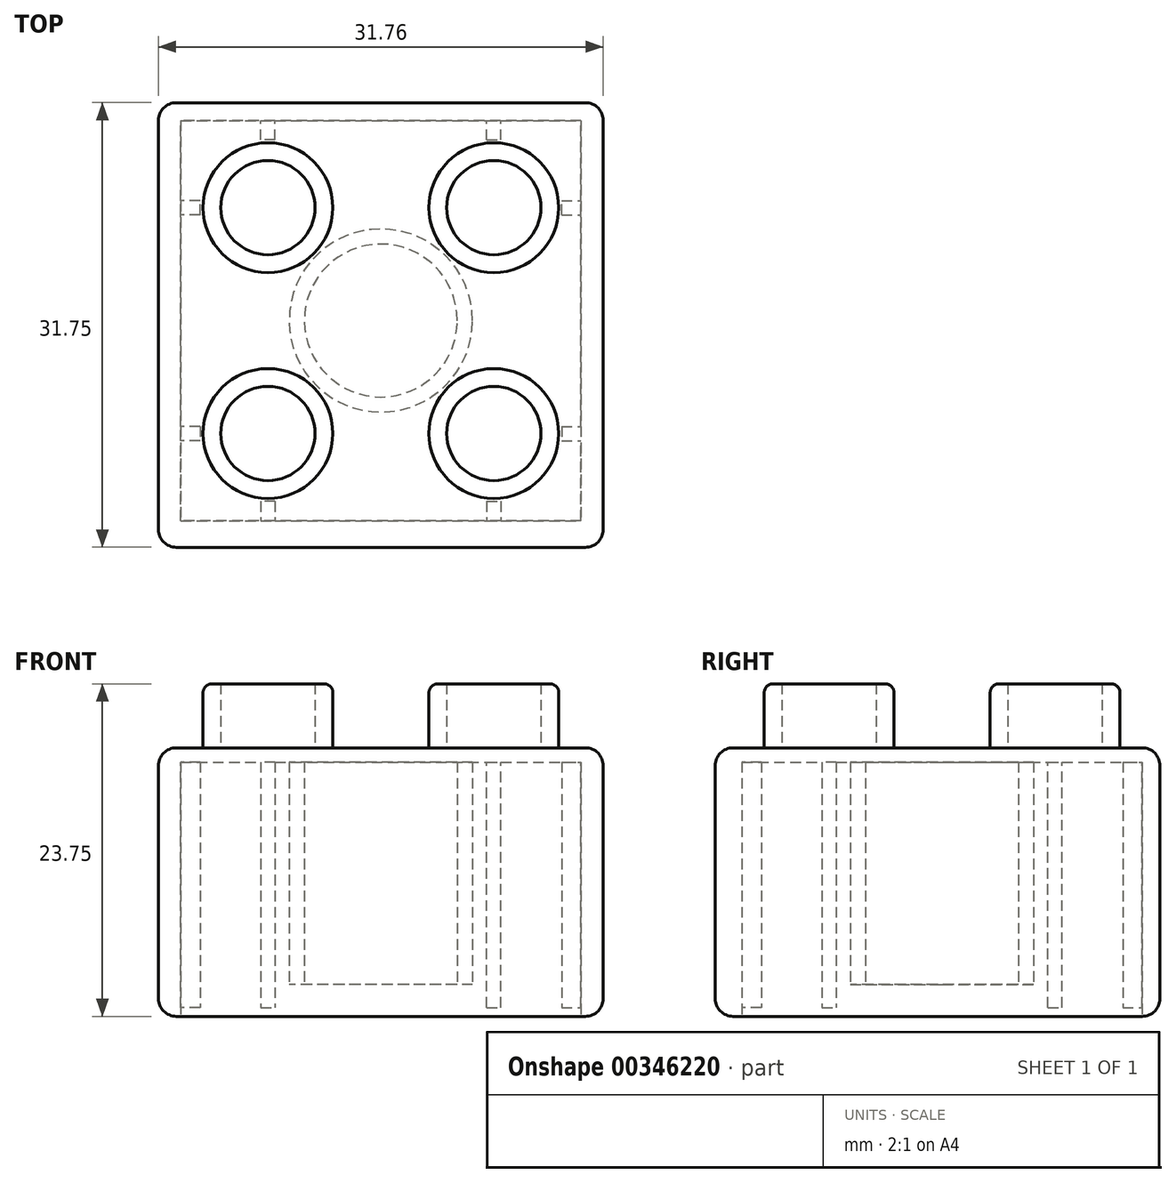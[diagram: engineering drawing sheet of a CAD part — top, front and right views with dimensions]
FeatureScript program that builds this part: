
annotation { "Feature Type Name" : "Feature", "Feature Type Description" : "" }
export const myFeature = defineFeature(function(context is Context, id is Id, definition is map)
    precondition{}
    {
        {
            var Q0;
            Q0=qCreatedBy(makeId("Top.planeOp"),FACE);
            var sketch = newSketch(context, id + "F0", { "sketchPlane" : qUnion([Q0])});
            skPoint(sketch, "E0", {"position": v(0, 16.87) * mm});
            skPoint(sketch, "E1", {"position": v(0, 15.88) * mm});
            skPoint(sketch, "E2", {"position": v(0, -14.88) * mm});
            skPoint(sketch, "E3", {"position": v(0, -15.88) * mm});
            skPoint(sketch, "E4", {"position": v(17.1, 0) * mm});
            skPoint(sketch, "E5", {"position": v(15.88, 0) * mm});
            skPoint(sketch, "E6", {"position": v(-15.88, 0) * mm});
            skPoint(sketch, "E7", {"position": v(15.64, 15.88) * mm});
            skPoint(sketch, "E8", {"position": v(15.88, 15.56) * mm});
            skPoint(sketch, "E9", {"position": v(-16.3, -15.88) * mm});
            skPoint(sketch, "E10", {"position": v(-15.88, -16.2) * mm});
            skLineSegment(sketch, "E11.bottom", {"start": v(-15.88, -16.2) * mm, "end": v(15.88, -16.2) * mm});
            skLineSegment(sketch, "E11.top", {"start": v(-15.88, 15.56) * mm, "end": v(15.88, 15.56) * mm});
            skLineSegment(sketch, "E11.left", {"start": v(-15.88, -16.2) * mm, "end": v(-15.88, 15.56) * mm});
            skLineSegment(sketch, "E11.right", {"start": v(15.88, -16.2) * mm, "end": v(15.88, 15.56) * mm});
            skSolve(sketch);
        }
        {
            var Q0;
            Q0=makeQuery(id+"F0.imprint","IMPRINT",FACE,{"disambiguationData":[TD([[makeQuery(id+"F0.imprint","IMPRINT",EDGE,{"derivedFrom":sQuery(id+"F0.wireOp",EDGE,"E11.bottom")}),1.0]])]});
            var sketch = newSketch(context, id + "F1", { "sketchPlane" : qUnion([Q0])});
            skPoint(sketch, "E12", {"position": v(14.77, 0) * mm});
            skPoint(sketch, "E13", {"position": v(14.29, 0) * mm});
            skPoint(sketch, "E14", {"position": v(-14.29, 0) * mm});
            skPoint(sketch, "E15", {"position": v(-14.29, -14.92) * mm});
            skPoint(sketch, "E16", {"position": v(-14.29, -14.29) * mm});
            skPoint(sketch, "E17", {"position": v(14.29, 14.33) * mm});
            skPoint(sketch, "E18", {"position": v(14.29, 14.29) * mm});
            skLineSegment(sketch, "E19.bottom", {"start": v(-14.29, -14.29) * mm, "end": v(14.29, -14.29) * mm});
            skLineSegment(sketch, "E19.top", {"start": v(-14.29, 14.29) * mm, "end": v(14.29, 14.29) * mm});
            skLineSegment(sketch, "E19.left", {"start": v(-14.29, -14.29) * mm, "end": v(-14.29, 14.29) * mm});
            skLineSegment(sketch, "E19.right", {"start": v(14.29, -14.29) * mm, "end": v(14.29, 14.29) * mm});
            skSolve(sketch);
        }
        {
            var Q0;
            Q0=makeQuery(id+"F1.imprint","IMPRINT",FACE,{"disambiguationData":[TD([[makeQuery(id+"F1.imprint","IMPRINT",EDGE,{"derivedFrom":sQuery(id+"F1.wireOp",EDGE,"E19.bottom")}),1.0]])]});
            var sketch = newSketch(context, id + "F2", { "sketchPlane" : qUnion([Q0])});
            skPoint(sketch, "E20", {"position": v(0, 0) * mm});
            skCircle(sketch, "E21", {"center": v(0, 0) * mm, "radius": 6.54 * mm});
            skSolve(sketch);
        }
        {
            var Q0;
            Q0=makeQuery(id+"F1.imprint","IMPRINT",FACE,{"disambiguationData":[TD([[makeQuery(id+"F1.imprint","IMPRINT",EDGE,{"derivedFrom":sQuery(id+"F1.wireOp",EDGE,"E19.bottom")}),1.0]])]});
            var sketch = newSketch(context, id + "F3", { "sketchPlane" : qUnion([Q0])});
            skPoint(sketch, "E22", {"position": v(0, 0) * mm});
            skCircle(sketch, "E23", {"center": v(0, 0) * mm, "radius": 5.46 * mm});
            skSolve(sketch);
        }
        {
            var Q0;
            Q0=makeQuery(id+"F1.imprint","IMPRINT",FACE,{"disambiguationData":[TD([[makeQuery(id+"F1.imprint","IMPRINT",EDGE,{"derivedFrom":sQuery(id+"F1.wireOp",EDGE,"E19.bottom")}),1.0]])]});
            var sketch = newSketch(context, id + "F4", { "sketchPlane" : qUnion([Q0])});
            skPoint(sketch, "E24", {"position": v(0, 1.02) * mm});
            skPoint(sketch, "E25", {"position": v(0, 0.95) * mm});
            skPoint(sketch, "E26", {"position": v(0, -0.95) * mm});
            skPoint(sketch, "E27", {"position": v(-0.23, 0) * mm});
            skPoint(sketch, "E28", {"position": v(-0.5, 0) * mm});
            skPoint(sketch, "E29", {"position": v(0.3, 0) * mm});
            skPoint(sketch, "E30", {"position": v(0.5, 0) * mm});
            skPoint(sketch, "E31", {"position": v(-0.5, -0.86) * mm});
            skPoint(sketch, "E32", {"position": v(-0.5, -0.95) * mm});
            skPoint(sketch, "E33", {"position": v(0.5, 0.95) * mm});
            skLineSegment(sketch, "E34.bottom", {"start": v(-0.5, -0.95) * mm, "end": v(0.5, -0.95) * mm});
            skLineSegment(sketch, "E34.top", {"start": v(-0.5, 0.95) * mm, "end": v(0.5, 0.95) * mm});
            skLineSegment(sketch, "E34.left", {"start": v(-0.5, -0.95) * mm, "end": v(-0.5, 0.95) * mm});
            skLineSegment(sketch, "E34.right", {"start": v(0.5, -0.95) * mm, "end": v(0.5, 0.95) * mm});
            skSolve(sketch);
        }
        {
            var Q0;
            Q0=qSketchRegion(id+"F0",true);
            extrude(context, id + "F5", {"entities" : qUnion([Q0]), "depth" : 19.18 * mm});
        }
        {
            var Q0;
            Q0=qSketchRegion(id+"F1",true);
            extrude(context, id + "F6", {"entities" : qUnion([Q0]), "operationType" : NewBodyOperationType.REMOVE, "depth" : 18.16 * mm, "hasSecondDirection" : true, "secondDirectionOppositeDirection" : true, "secondDirectionDepth" : 0.38 * mm});
        }
        {
            var Q0;
            Q0=qSketchRegion(id+"F2",true);
            extrude(context, id + "F7", {"entities" : qUnion([Q0]), "operationType" : NewBodyOperationType.ADD, "depth" : 15.88 * mm});
        }
        {
            var Q0;
            Q0=qSketchRegion(id+"F3",true);
            extrude(context, id + "F8", {"entities" : qUnion([Q0]), "operationType" : NewBodyOperationType.REMOVE, "depth" : 15.88 * mm, "hasSecondDirection" : true, "secondDirectionOppositeDirection" : true, "secondDirectionDepth" : 0.64 * mm});
        }
        {
            var Q0;
            Q0=makeQuery(id+"F7.opExtrude","SWEPT_BODY",BODY,{"disambiguationData":[OSD([sQuery(id+"F2.wireOp",EDGE,"E21")])]});
            transform(context, id + "F9", {"entities" : qUnion([Q0]), "transformType" : TransformType.TRANSLATION_3D, "dx" : 0 * mm, "dy" : 0 * mm, "dz" : 2.3 * mm, "makeCopy" : false});
        }
        {
            var Q0;
            Q0=makeQuery(id+"F4.imprint","IMPRINT",FACE,{"disambiguationData":[TD([[makeQuery(id+"F4.imprint","IMPRINT",EDGE,{"derivedFrom":sQuery(id+"F4.wireOp",EDGE,"E34.bottom")}),1.0]])]});
            extrude(context, id + "F10", {"entities" : qUnion([Q0]), "operationType" : NewBodyOperationType.ADD, "depth" : 17.53 * mm});
        }
        {
            var Q0;
            Q0=makeQuery(id+"F10.opExtrude","SWEPT_BODY",BODY,{"disambiguationData":[OSD([sQuery(id+"F4.wireOp",EDGE,"E34.bottom"),sQuery(id+"F4.wireOp",EDGE,"E34.top"),sQuery(id+"F4.wireOp",EDGE,"E34.left"),sQuery(id+"F4.wireOp",EDGE,"E34.right")])]});
            transform(context, id + "F11", {"entities" : qUnion([Q0]), "transformType" : TransformType.TRANSLATION_3D, "dx" : 8.06 * mm, "dy" : 13.86 * mm, "dz" : 0.64 * mm, "makeCopy" : false});
        }
        {
            var Q0;
            Q0=makeQuery(id+"F10.opExtrude","SWEPT_BODY",BODY,{"disambiguationData":[OSD([sQuery(id+"F4.wireOp",EDGE,"E34.bottom"),sQuery(id+"F4.wireOp",EDGE,"E34.top"),sQuery(id+"F4.wireOp",EDGE,"E34.left"),sQuery(id+"F4.wireOp",EDGE,"E34.right")])]});
            var Q1;
            Q1=qCreatedBy(makeId("Front.planeOp"),FACE);
            mirror(context, id + "F12", {"entities" : qUnion([Q0]), "mirrorPlane" : qUnion([Q1])});
        }
        {
            var Q0;
            Q0=makeQuery(id+"F12.opPattern","COPY",BODY,{"derivedFrom":makeQuery(id+"F10.opExtrude","SWEPT_BODY",BODY,{"disambiguationData":[OSD([sQuery(id+"F4.wireOp",EDGE,"E34.bottom"),sQuery(id+"F4.wireOp",EDGE,"E34.top"),sQuery(id+"F4.wireOp",EDGE,"E34.left"),sQuery(id+"F4.wireOp",EDGE,"E34.right")])]}),"instanceName":"1"});
            var Q1;
            Q1=makeQuery(id+"F10.opExtrude","SWEPT_BODY",BODY,{"disambiguationData":[OSD([sQuery(id+"F4.wireOp",EDGE,"E34.bottom"),sQuery(id+"F4.wireOp",EDGE,"E34.top"),sQuery(id+"F4.wireOp",EDGE,"E34.left"),sQuery(id+"F4.wireOp",EDGE,"E34.right")])]});
            var Q2;
            Q2=qCreatedBy(makeId("Right.planeOp"),FACE);
            mirror(context, id + "F13", {"entities" : qUnion([Q0, Q1]), "mirrorPlane" : qUnion([Q2])});
        }
        {
            var Q0;
            Q0=qCreatedBy(makeId("Front.planeOp"),FACE);
            var sketch = newSketch(context, id + "F14", { "sketchPlane" : qUnion([Q0])});
            skLineSegment(sketch, "E35", {"start": v(0, 40.9) * mm, "end": v(0, -32.36) * mm});
            skSolve(sketch);
        }
        {
            var Q0;
            Q0=makeQuery(id+"F12.opPattern","COPY",BODY,{"derivedFrom":makeQuery(id+"F10.opExtrude","SWEPT_BODY",BODY,{"disambiguationData":[OSD([sQuery(id+"F4.wireOp",EDGE,"E34.bottom"),sQuery(id+"F4.wireOp",EDGE,"E34.top"),sQuery(id+"F4.wireOp",EDGE,"E34.left"),sQuery(id+"F4.wireOp",EDGE,"E34.right")])]}),"instanceName":"1"});
            var Q1;
            Q1=makeQuery(id+"F13.opPattern","COPY",BODY,{"derivedFrom":makeQuery(id+"F12.opPattern","COPY",BODY,{"derivedFrom":makeQuery(id+"F10.opExtrude","SWEPT_BODY",BODY,{"disambiguationData":[OSD([sQuery(id+"F4.wireOp",EDGE,"E34.bottom"),sQuery(id+"F4.wireOp",EDGE,"E34.top"),sQuery(id+"F4.wireOp",EDGE,"E34.left"),sQuery(id+"F4.wireOp",EDGE,"E34.right")])]}),"instanceName":"1"}),"instanceName":"1"});
            var Q2;
            Q2=makeQuery(id+"F10.opExtrude","SWEPT_BODY",BODY,{"disambiguationData":[OSD([sQuery(id+"F4.wireOp",EDGE,"E34.bottom"),sQuery(id+"F4.wireOp",EDGE,"E34.top"),sQuery(id+"F4.wireOp",EDGE,"E34.left"),sQuery(id+"F4.wireOp",EDGE,"E34.right")])]});
            var Q3;
            Q3=makeQuery(id+"F13.opPattern","COPY",BODY,{"derivedFrom":makeQuery(id+"F10.opExtrude","SWEPT_BODY",BODY,{"disambiguationData":[OSD([sQuery(id+"F4.wireOp",EDGE,"E34.bottom"),sQuery(id+"F4.wireOp",EDGE,"E34.top"),sQuery(id+"F4.wireOp",EDGE,"E34.left"),sQuery(id+"F4.wireOp",EDGE,"E34.right")])]}),"instanceName":"1"});
            var Q4;
            Q4=sQuery(id+"F14.wireOp",EDGE,"E35");
            transform(context, id + "F15", {"entities" : qUnion([Q0, Q1, Q2, Q3]), "transformType" : TransformType.ROTATION, "transformAxis" : qUnion([Q4]), "angle" : 90 * degree, "makeCopy" : true});
        }
        {
            var Q0;
            Q0=qCreatedBy(makeId("Top.planeOp"),FACE);
            var sketch = newSketch(context, id + "F16", { "sketchPlane" : qUnion([Q0])});
            skCircle(sketch, "E36", {"center": v(0, 0) * mm, "radius": 4.64 * mm});
            skSolve(sketch);
        }
        {
            var Q0;
            Q0=qCreatedBy(makeId("Top.planeOp"),FACE);
            var sketch = newSketch(context, id + "F17", { "sketchPlane" : qUnion([Q0])});
            skCircle(sketch, "E37", {"center": v(0, 0) * mm, "radius": 3.37 * mm});
            skSolve(sketch);
        }
        {
            var Q0;
            Q0=makeQuery(id+"F16.imprint","IMPRINT",FACE,{"disambiguationData":[TD([[makeQuery(id+"F16.imprint","IMPRINT",EDGE,{"derivedFrom":sQuery(id+"F16.wireOp",EDGE,"E36")}),1.0]])]});
            extrude(context, id + "F18", {"entities" : qUnion([Q0]), "depth" : 4.7 * mm});
        }
        {
            var Q0;
            Q0=makeQuery(id+"F17.imprint","IMPRINT",FACE,{"disambiguationData":[TD([[makeQuery(id+"F17.imprint","IMPRINT",EDGE,{"derivedFrom":sQuery(id+"F17.wireOp",EDGE,"E37")}),1.0]])]});
            extrude(context, id + "F19", {"entities" : qUnion([Q0]), "operationType" : NewBodyOperationType.REMOVE, "depth" : 4.7 * mm});
        }
        {
            var Q0;
            Q0=makeQuery(id+"F18.opExtrude","SWEPT_BODY",BODY,{"disambiguationData":[OSD([sQuery(id+"F16.wireOp",EDGE,"E36")])]});
            transform(context, id + "F20", {"entities" : qUnion([Q0]), "transformType" : TransformType.TRANSLATION_3D, "dx" : 8.06 * mm, "dy" : 8.06 * mm, "dz" : 19.05 * mm, "makeCopy" : false});
        }
        {
            var Q0;
            Q0=makeQuery(id+"F18.opExtrude","SWEPT_BODY",BODY,{"disambiguationData":[OSD([sQuery(id+"F16.wireOp",EDGE,"E36")])]});
            var Q1;
            Q1=qCreatedBy(makeId("Front.planeOp"),FACE);
            mirror(context, id + "F21", {"entities" : qUnion([Q0]), "mirrorPlane" : qUnion([Q1])});
        }
        {
            var Q0;
            Q0=makeQuery(id+"F18.opExtrude","SWEPT_BODY",BODY,{"disambiguationData":[OSD([sQuery(id+"F16.wireOp",EDGE,"E36")])]});
            var Q1;
            Q1=makeQuery(id+"F21.opPattern","COPY",BODY,{"derivedFrom":makeQuery(id+"F18.opExtrude","SWEPT_BODY",BODY,{"disambiguationData":[OSD([sQuery(id+"F16.wireOp",EDGE,"E36")])]}),"instanceName":"1"});
            var Q2;
            Q2=qCreatedBy(makeId("Right.planeOp"),FACE);
            mirror(context, id + "F22", {"entities" : qUnion([Q0, Q1]), "mirrorPlane" : qUnion([Q2])});
        }
        {
            var Q0;
            Q0=makeQuery(id+"F5.opExtrude","CAP_EDGE",EDGE,{"disambiguationData":[OSD([sQuery(id+"F0.wireOp",EDGE,"E11.bottom")])],"isStart":false});
            var Q1;
            Q1=makeQuery(id+"F5.opExtrude","CAP_EDGE",EDGE,{"disambiguationData":[OSD([sQuery(id+"F0.wireOp",EDGE,"E11.left")])],"isStart":false});
            var Q2;
            Q2=makeQuery(id+"F5.opExtrude","CAP_EDGE",EDGE,{"disambiguationData":[OSD([sQuery(id+"F0.wireOp",EDGE,"E11.top")])],"isStart":false});
            var Q3;
            Q3=makeQuery(id+"F5.opExtrude","CAP_EDGE",EDGE,{"disambiguationData":[OSD([sQuery(id+"F0.wireOp",EDGE,"E11.right")])],"isStart":false});
            var Q4;
            Q4=makeQuery(id+"F5.opExtrude","SWEPT_EDGE",EDGE,{"disambiguationData":[OSD([sQuery(id+"F0.wireOp",EDGE,"E11.bottom"),sQuery(id+"F0.wireOp",EDGE,"E11.left")])]});
            var Q5;
            Q5=makeQuery(id+"F5.opExtrude","SWEPT_EDGE",EDGE,{"disambiguationData":[OSD([sQuery(id+"F0.wireOp",EDGE,"E11.bottom"),sQuery(id+"F0.wireOp",EDGE,"E11.right")])]});
            var Q6;
            Q6=makeQuery(id+"F5.opExtrude","SWEPT_EDGE",EDGE,{"disambiguationData":[OSD([sQuery(id+"F0.wireOp",EDGE,"E11.top"),sQuery(id+"F0.wireOp",EDGE,"E11.left")])]});
            var Q7;
            Q7=makeQuery(id+"F5.opExtrude","SWEPT_EDGE",EDGE,{"disambiguationData":[OSD([sQuery(id+"F0.wireOp",EDGE,"E11.top"),sQuery(id+"F0.wireOp",EDGE,"E11.right")])]});
            var Q8;
            Q8=makeQuery(id+"F5.opExtrude","CAP_EDGE",EDGE,{"disambiguationData":[OSD([sQuery(id+"F0.wireOp",EDGE,"E11.right")])],"isStart":true});
            var Q9;
            Q9=makeQuery(id+"F5.opExtrude","CAP_EDGE",EDGE,{"disambiguationData":[OSD([sQuery(id+"F0.wireOp",EDGE,"E11.bottom")])],"isStart":true});
            var Q10;
            Q10=makeQuery(id+"F5.opExtrude","CAP_EDGE",EDGE,{"disambiguationData":[OSD([sQuery(id+"F0.wireOp",EDGE,"E11.left")])],"isStart":true});
            var Q11;
            Q11=makeQuery(id+"F5.opExtrude","CAP_EDGE",EDGE,{"disambiguationData":[OSD([sQuery(id+"F0.wireOp",EDGE,"E11.top")])],"isStart":true});
            fillet(context, id + "F23", {"entities" : qUnion([Q0, Q1, Q2, Q3, Q4, Q5, Q6, Q7, Q8, Q9, Q10, Q11]), "radius" : 1.27 * mm, "tangentPropagation" : true, "allowEdgeOverflow" : false});
        }
        {
            var Q0;
            Q0=makeQuery(id+"F22.opPattern","COPY",EDGE,{"derivedFrom":makeQuery(id+"F18.opExtrude","CAP_EDGE",EDGE,{"disambiguationData":[OSD([sQuery(id+"F16.wireOp",EDGE,"E36")])],"isStart":false}),"instanceName":"1"});
            var Q1;
            Q1=makeQuery(id+"F18.opExtrude","CAP_EDGE",EDGE,{"disambiguationData":[OSD([sQuery(id+"F16.wireOp",EDGE,"E36")])],"isStart":false});
            var Q2;
            Q2=makeQuery(id+"F21.opPattern","COPY",EDGE,{"derivedFrom":makeQuery(id+"F18.opExtrude","CAP_EDGE",EDGE,{"disambiguationData":[OSD([sQuery(id+"F16.wireOp",EDGE,"E36")])],"isStart":false}),"instanceName":"1"});
            var Q3;
            Q3=makeQuery(id+"F22.opPattern","COPY",EDGE,{"derivedFrom":makeQuery(id+"F21.opPattern","COPY",EDGE,{"derivedFrom":makeQuery(id+"F18.opExtrude","CAP_EDGE",EDGE,{"disambiguationData":[OSD([sQuery(id+"F16.wireOp",EDGE,"E36")])],"isStart":false}),"instanceName":"1"}),"instanceName":"1"});
            fillet(context, id + "F24", {"entities" : qUnion([Q0, Q1, Q2, Q3]), "radius" : 0.64 * mm, "tangentPropagation" : true, "allowEdgeOverflow" : false});
        }
        {
            var Q0;
            Q0=makeQuery(id+"F15.opPattern","COPY",BODY,{"derivedFrom":makeQuery(id+"F10.opExtrude","SWEPT_BODY",BODY,{"disambiguationData":[OSD([sQuery(id+"F4.wireOp",EDGE,"E34.bottom"),sQuery(id+"F4.wireOp",EDGE,"E34.top"),sQuery(id+"F4.wireOp",EDGE,"E34.left"),sQuery(id+"F4.wireOp",EDGE,"E34.right")])]}),"instanceName":"1"});
            var Q1;
            Q1=makeQuery(id+"F21.opPattern","COPY",BODY,{"derivedFrom":makeQuery(id+"F18.opExtrude","SWEPT_BODY",BODY,{"disambiguationData":[OSD([sQuery(id+"F16.wireOp",EDGE,"E36")])]}),"instanceName":"1"});
            var Q2;
            Q2=makeQuery(id+"F5.opExtrude","SWEPT_BODY",BODY,{"disambiguationData":[OSD([sQuery(id+"F0.wireOp",EDGE,"E11.bottom"),sQuery(id+"F0.wireOp",EDGE,"E11.top"),sQuery(id+"F0.wireOp",EDGE,"E11.left"),sQuery(id+"F0.wireOp",EDGE,"E11.right")])]});
            var Q3;
            Q3=makeQuery(id+"F7.opExtrude","SWEPT_BODY",BODY,{"disambiguationData":[OSD([sQuery(id+"F2.wireOp",EDGE,"E21")])]});
            var Q4;
            Q4=makeQuery(id+"F12.opPattern","COPY",BODY,{"derivedFrom":makeQuery(id+"F10.opExtrude","SWEPT_BODY",BODY,{"disambiguationData":[OSD([sQuery(id+"F4.wireOp",EDGE,"E34.bottom"),sQuery(id+"F4.wireOp",EDGE,"E34.top"),sQuery(id+"F4.wireOp",EDGE,"E34.left"),sQuery(id+"F4.wireOp",EDGE,"E34.right")])]}),"instanceName":"1"});
            var Q5;
            Q5=makeQuery(id+"F13.opPattern","COPY",BODY,{"derivedFrom":makeQuery(id+"F10.opExtrude","SWEPT_BODY",BODY,{"disambiguationData":[OSD([sQuery(id+"F4.wireOp",EDGE,"E34.bottom"),sQuery(id+"F4.wireOp",EDGE,"E34.top"),sQuery(id+"F4.wireOp",EDGE,"E34.left"),sQuery(id+"F4.wireOp",EDGE,"E34.right")])]}),"instanceName":"1"});
            var Q6;
            Q6=makeQuery(id+"F13.opPattern","COPY",BODY,{"derivedFrom":makeQuery(id+"F12.opPattern","COPY",BODY,{"derivedFrom":makeQuery(id+"F10.opExtrude","SWEPT_BODY",BODY,{"disambiguationData":[OSD([sQuery(id+"F4.wireOp",EDGE,"E34.bottom"),sQuery(id+"F4.wireOp",EDGE,"E34.top"),sQuery(id+"F4.wireOp",EDGE,"E34.left"),sQuery(id+"F4.wireOp",EDGE,"E34.right")])]}),"instanceName":"1"}),"instanceName":"1"});
            var Q7;
            Q7=makeQuery(id+"F15.opPattern","COPY",BODY,{"derivedFrom":makeQuery(id+"F12.opPattern","COPY",BODY,{"derivedFrom":makeQuery(id+"F10.opExtrude","SWEPT_BODY",BODY,{"disambiguationData":[OSD([sQuery(id+"F4.wireOp",EDGE,"E34.bottom"),sQuery(id+"F4.wireOp",EDGE,"E34.top"),sQuery(id+"F4.wireOp",EDGE,"E34.left"),sQuery(id+"F4.wireOp",EDGE,"E34.right")])]}),"instanceName":"1"}),"instanceName":"1"});
            var Q8;
            Q8=makeQuery(id+"F15.opPattern","COPY",BODY,{"derivedFrom":makeQuery(id+"F13.opPattern","COPY",BODY,{"derivedFrom":makeQuery(id+"F10.opExtrude","SWEPT_BODY",BODY,{"disambiguationData":[OSD([sQuery(id+"F4.wireOp",EDGE,"E34.bottom"),sQuery(id+"F4.wireOp",EDGE,"E34.top"),sQuery(id+"F4.wireOp",EDGE,"E34.left"),sQuery(id+"F4.wireOp",EDGE,"E34.right")])]}),"instanceName":"1"}),"instanceName":"1"});
            var Q9;
            Q9=makeQuery(id+"F15.opPattern","COPY",BODY,{"derivedFrom":makeQuery(id+"F13.opPattern","COPY",BODY,{"derivedFrom":makeQuery(id+"F12.opPattern","COPY",BODY,{"derivedFrom":makeQuery(id+"F10.opExtrude","SWEPT_BODY",BODY,{"disambiguationData":[OSD([sQuery(id+"F4.wireOp",EDGE,"E34.bottom"),sQuery(id+"F4.wireOp",EDGE,"E34.top"),sQuery(id+"F4.wireOp",EDGE,"E34.left"),sQuery(id+"F4.wireOp",EDGE,"E34.right")])]}),"instanceName":"1"}),"instanceName":"1"}),"instanceName":"1"});
            var Q10;
            Q10=makeQuery(id+"F18.opExtrude","SWEPT_BODY",BODY,{"disambiguationData":[OSD([sQuery(id+"F16.wireOp",EDGE,"E36")])]});
            var Q11;
            Q11=makeQuery(id+"F22.opPattern","COPY",BODY,{"derivedFrom":makeQuery(id+"F18.opExtrude","SWEPT_BODY",BODY,{"disambiguationData":[OSD([sQuery(id+"F16.wireOp",EDGE,"E36")])]}),"instanceName":"1"});
            var Q12;
            Q12=makeQuery(id+"F22.opPattern","COPY",BODY,{"derivedFrom":makeQuery(id+"F21.opPattern","COPY",BODY,{"derivedFrom":makeQuery(id+"F18.opExtrude","SWEPT_BODY",BODY,{"disambiguationData":[OSD([sQuery(id+"F16.wireOp",EDGE,"E36")])]}),"instanceName":"1"}),"instanceName":"1"});
            var Q13;
            Q13=makeQuery(id+"F10.opExtrude","SWEPT_BODY",BODY,{"disambiguationData":[OSD([sQuery(id+"F4.wireOp",EDGE,"E34.bottom"),sQuery(id+"F4.wireOp",EDGE,"E34.top"),sQuery(id+"F4.wireOp",EDGE,"E34.left"),sQuery(id+"F4.wireOp",EDGE,"E34.right")])]});
            booleanBodies(context, id + "F25", {"operationType" : BooleanOperationType.UNION, "tools" : qUnion([Q0, Q1, Q2, Q3, Q4, Q5, Q6, Q7, Q8, Q9, Q10, Q11, Q12, Q13])});
        }
    });
